# Revit family: AFX-Kirian-Pendant+
name_source: partatom
category: Lighting Fixtures
units: mm (PartAtom-declared; Revit-internal decimal feet)

## family parameters
Cut with Voids When Loaded = No
Host = Face
Light Source = Yes
Part Type = Normal
Room Calculation Point = No
Round Connector Dimension = Use Diameter
Shared = No

## types (1)
- KRNP04
    Apparent Load = 0 VA
    Assembly Code = D5020200
    Body Finish = AFX - Glass, Cast, Gray
    Bracket Finish = AFX - Aluminum Black
    Cable Finish = AFX - Aluminum Black
    Color Filter = 16777215
    Color Rendering Index = 90
    Colour Rendering Index = 90 CRI
    Default Elevation = 48"
    Description = 4" LED Pendant
    Diameter = 4"
    Diffuser Finish = AFX - White Acrylic
    Dimming Lamp Color Temperature Shift = <None>
    Emit Shape Visible in Rendering = No
    Emit from Circle Diameter = 24"
    Height = 9 3/4"
    Lamp = LED
    Manufacturer = AFX Inc
    Model = KRNP04
    Photometric Web File = KRNP04L30D1BK_3000K_IES.IES
    Product Documentation Link = https://www.afxinc.com
    Revit Model Built By = https://servex-us.com
    Tilt Angle = 90.00°
    Type Comments = GLO
    URL = https://www.afxinc.com
    Voltage = 120 V
    Wattage Comments = 6W

## geometry (parser evidence)
native form markers: Sweep x2
no freeform markers — native parametric forms only
